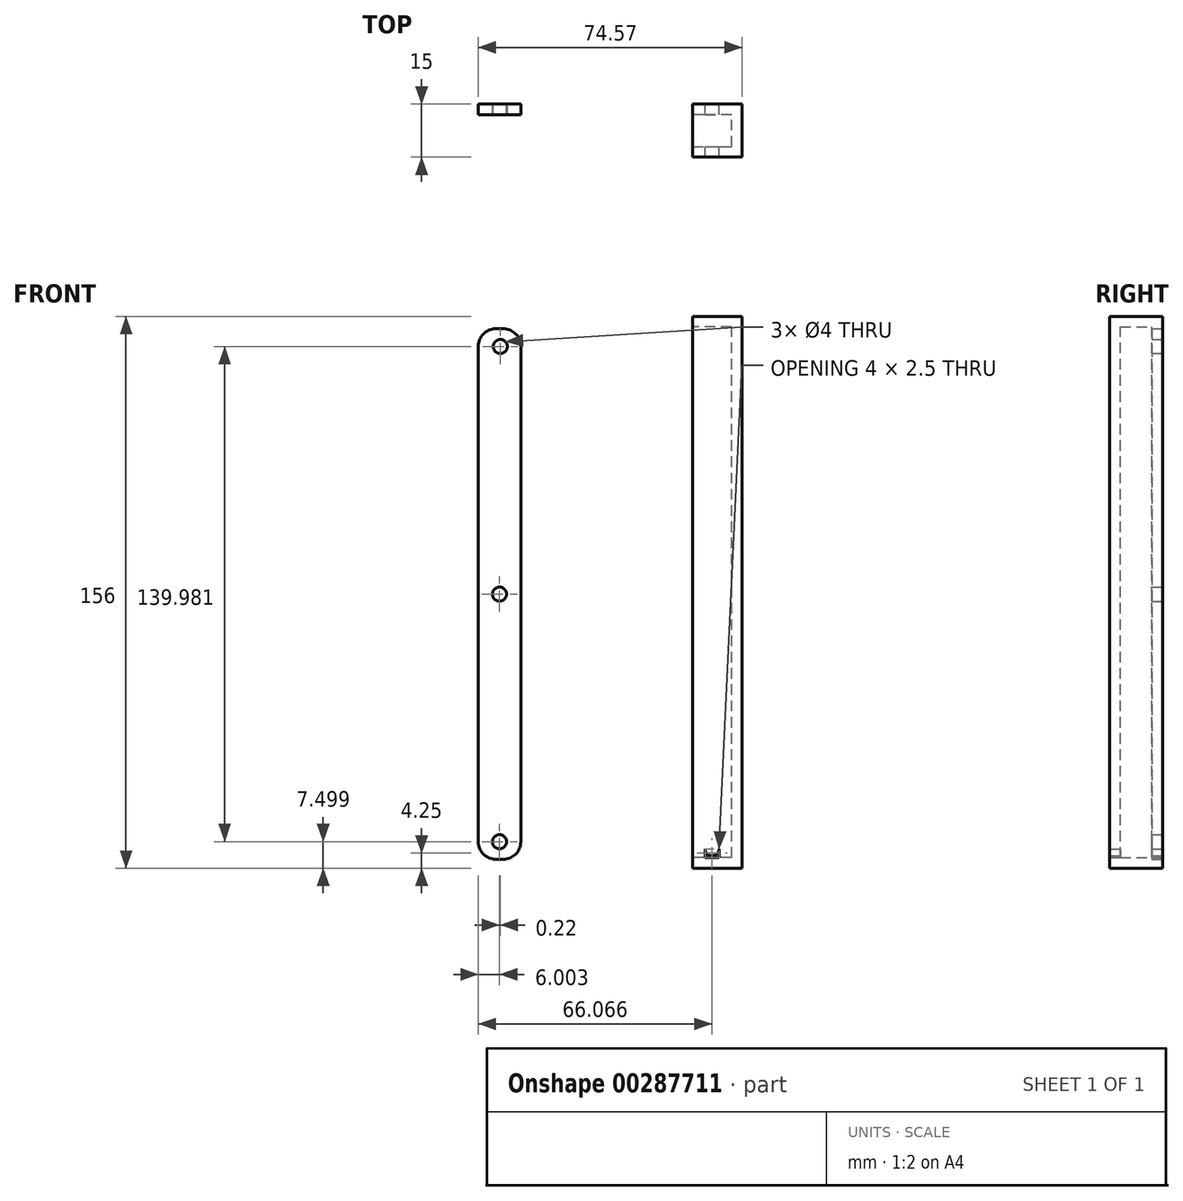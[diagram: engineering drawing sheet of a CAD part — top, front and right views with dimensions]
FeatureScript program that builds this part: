
annotation { "Feature Type Name" : "Feature", "Feature Type Description" : "" }
export const myFeature = defineFeature(function(context is Context, id is Id, definition is map)
    precondition{}
    {
        {
            var Q0;
            Q0=qCreatedBy(makeId("Front.planeOp"),FACE);
            var sketch = newSketch(context, id + "F0", { "sketchPlane" : qUnion([Q0])});
            skLineSegment(sketch, "E0.bottom", {"start": v(-38.84, 75.02) * mm, "end": v(-36.84, 75.02) * mm});
            skLineSegment(sketch, "E0.top", {"start": v(-38.84, -74.98) * mm, "end": v(-36.84, -74.98) * mm});
            skLineSegment(sketch, "E0.left", {"start": v(-43.84, 70.02) * mm, "end": v(-43.84, -69.98) * mm});
            skLineSegment(sketch, "E0.right", {"start": v(-31.84, 70.02) * mm, "end": v(-31.84, -69.98) * mm});
            skPoint(sketch, "E1.visualSharp", {"position": v(-43.84, 75.02) * mm});
            skArc(sketch, "E1.filletArc", {"start": v(-38.84, 75.02) * mm, "mid": v(-42.37, 73.55) * mm, "end": v(-43.84, 70.02) * mm});
            skPoint(sketch, "E2.visualSharp", {"position": v(-31.84, 75.02) * mm});
            skArc(sketch, "E2.filletArc", {"start": v(-31.84, 70.02) * mm, "mid": v(-33.3, 73.55) * mm, "end": v(-36.84, 75.02) * mm});
            skPoint(sketch, "E3.visualSharp", {"position": v(-43.84, -74.98) * mm});
            skArc(sketch, "E3.filletArc", {"start": v(-43.84, -69.98) * mm, "mid": v(-42.37, -73.52) * mm, "end": v(-38.84, -74.98) * mm});
            skPoint(sketch, "E4.visualSharp", {"position": v(-31.84, -74.98) * mm});
            skArc(sketch, "E4.filletArc", {"start": v(-36.84, -74.98) * mm, "mid": v(-33.3, -73.52) * mm, "end": v(-31.84, -69.98) * mm});
            skLineSegment(sketch, "E5", {"start": v(-37.84, -74.98) * mm, "end": v(-37.84, -69.98) * mm, "construction": true});
            skCircle(sketch, "E6", {"center": v(-37.84, -69.98) * mm, "radius": 2 * mm});
            skLineSegment(sketch, "E7", {"start": v(-43.84, 0.02) * mm, "end": v(-31.84, 0) * mm, "construction": true});
            skCircle(sketch, "E8.MirrorC", {"center": v(-37.62, 70) * mm, "radius": 2 * mm});
            skLineSegment(sketch, "E9.left", {"start": v(18.73, 70.52) * mm, "end": v(18.73, -69.48) * mm});
            skLineSegment(sketch, "E9.right", {"start": v(30.73, 70.02) * mm, "end": v(30.73, -69.98) * mm});
            skPoint(sketch, "E10.visualSharp", {"position": v(18.73, 75.52) * mm});
            skPoint(sketch, "E11.visualSharp", {"position": v(30.73, 75.52) * mm});
            skPoint(sketch, "E12.visualSharp", {"position": v(18.73, -74.48) * mm});
            skPoint(sketch, "E13.visualSharp", {"position": v(30.73, -74.48) * mm});
            skLineSegment(sketch, "E14", {"start": v(30.73, -69.98) * mm, "end": v(30.73, -74.48) * mm});
            skLineSegment(sketch, "E15", {"start": v(18.73, -69.48) * mm, "end": v(18.73, -74.48) * mm});
            skLineSegment(sketch, "E16", {"start": v(18.73, 70.52) * mm, "end": v(18.73, 75.52) * mm});
            skLineSegment(sketch, "E17", {"start": v(30.73, 75.52) * mm, "end": v(30.73, 70.02) * mm});
            skLineSegment(sketch, "E18", {"start": v(27.73, 75.52) * mm, "end": v(27.73, -74.98) * mm});
            skLineSegment(sketch, "E19", {"start": v(30.73, -74.48) * mm, "end": v(18.73, -74.48) * mm});
            skLineSegment(sketch, "E20", {"start": v(30.73, 75.52) * mm, "end": v(18.73, 75.52) * mm});
            skLineSegment(sketch, "E21", {"start": v(20.23, 75.52) * mm, "end": v(20.23, -74.48) * mm});
            skLineSegment(sketch, "E22", {"start": v(24.23, -74.48) * mm, "end": v(24.23, 75.52) * mm});
            skLineSegment(sketch, "E23", {"start": v(24.23, 75.52) * mm, "end": v(20.23, 75.52) * mm, "construction": true});
            skPoint(sketch, "E24.startSnap0", {"position": v(22.23, 75.52) * mm});
            skLineSegment(sketch, "E25", {"start": v(24.23, -71.98) * mm, "end": v(20.23, -71.98) * mm, "construction": true});
            skLineSegment(sketch, "E26", {"start": v(24.23, 73.02) * mm, "end": v(20.23, 73.02) * mm, "construction": true});
            skLineSegment(sketch, "E27", {"start": v(22.23, -71.98) * mm, "end": v(22.23, 73.02) * mm, "construction": true});
            skArc(sketch, "E28.0.startCap", {"start": v(24.23, -71.98) * mm, "mid": v(22.23, -73.98) * mm, "end": v(20.23, -71.98) * mm});
            skArc(sketch, "E28.0.endCap", {"start": v(20.23, 73.02) * mm, "mid": v(22.23, 75.02) * mm, "end": v(24.23, 73.02) * mm});
            skLineSegment(sketch, "E28.0.left", {"start": v(20.23, -71.98) * mm, "end": v(20.23, 73.02) * mm});
            skLineSegment(sketch, "E28.0.right", {"start": v(24.23, -71.98) * mm, "end": v(24.23, 73.02) * mm});
            skCircle(sketch, "E29", {"center": v(-37.84, 0) * mm, "radius": 2 * mm});
            skSolve(sketch);
        }
        {
            var Q0;
            Q0=makeQuery(id+"F0.imprint","IMPRINT",FACE,{"disambiguationData":[TD([[makeQuery(id+"F0.imprint","IMPRINT",EDGE,{"derivedFrom":sQuery(id+"F0.wireOp",EDGE,"E0.bottom")}),-1.0]])]});
            extrude(context, id + "F1", {"entities" : qUnion([Q0]), "depth" : 3 * mm});
        }
        {
            var Q0;
            Q0=makeQuery(id+"F0.imprint","IMPRINT",FACE,{"disambiguationData":[TD([[makeQuery(id+"F0.imprint","IMPRINT",EDGE,{"derivedFrom":sQuery(id+"F0.wireOp",EDGE,"E9.right")}),-1.0]])]});
            var Q1;
            {var subQ0=sQuery(id+"F0.wireOp",EDGE,"E18");Q1=makeQuery(id+"F0.imprint","IMPRINT",FACE,{"disambiguationData":[TD([[makeQuery(id+"F0.imprint","IMPRINT",EDGE,{"derivedFrom":subQ0}),-1.0]])]});}
            var Q2;
            {var subQ0=sQuery(id+"F0.wireOp",EDGE,"E21");Q2=makeQuery(id+"F0.imprint","IMPRINT",FACE,{"disambiguationData":[TD([[makeQuery(id+"F0.imprint","IMPRINT",EDGE,{"derivedFrom":subQ0}),1.0]])]});}
            var Q3;
            Q3=makeQuery(id+"F0.imprint","IMPRINT",FACE,{"disambiguationData":[TD([[makeQuery(id+"F0.imprint","IMPRINT",EDGE,{"derivedFrom":sQuery(id+"F0.wireOp",EDGE,"E9.left")}),1.0]])]});
            extrude(context, id + "F2", {"entities" : qUnion([Q0, Q1, Q2, Q3]), "depth" : 3 * mm});
        }
        {
            var Q0;
            Q0=makeQuery(id+"F0.imprint","IMPRINT",FACE,{"disambiguationData":[TD([[makeQuery(id+"F0.imprint","IMPRINT",EDGE,{"derivedFrom":sQuery(id+"F0.wireOp",EDGE,"E9.right")}),-1.0]])]});
            extrude(context, id + "F3", {"entities" : qUnion([Q0]), "operationType" : NewBodyOperationType.ADD, "depth" : 15 * mm});
        }
        {
            var Q0;
            {var subQ0=sQuery(id+"F0.wireOp",EDGE,"E20");Q0=makeQuery(id+"F3.boolean.opBoolean","MERGE",FACE,{"derivedFrom":[makeQuery(id+"F2.opExtrude","SWEPT_FACE",FACE,{"disambiguationData":[OSD([subQ0])]}),makeQuery(id+"F3.opExtrude","SWEPT_FACE",FACE,{"disambiguationData":[OSD([subQ0])]})]});}
            var sketch = newSketch(context, id + "F4", { "sketchPlane" : qUnion([Q0])});
            skLineSegment(sketch, "E30.0", {"start": v(27.73, -15) * mm, "end": v(27.73, -3) * mm});
            skLineSegment(sketch, "E31", {"start": v(27.73, -15) * mm, "end": v(18.73, -15) * mm});
            skLineSegment(sketch, "E32", {"start": v(18.73, -15) * mm, "end": v(18.73, -12) * mm});
            skLineSegment(sketch, "E33", {"start": v(18.73, -12) * mm, "end": v(27.73, -12) * mm});
            skSolve(sketch);
        }
        {
            var Q0;
            {var subQ0=sQuery(id+"F4.wireOp",EDGE,"E31");Q0=makeQuery(id+"F4.imprint","IMPRINT",FACE,{"disambiguationData":[TD([[makeQuery(id+"F4.imprint","IMPRINT",EDGE,{"derivedFrom":subQ0}),-1.0]])]});}
            var Q1;
            {var subQ0=sQuery(id+"F0.wireOp",EDGE,"E19");Q1=makeQuery(id+"F3.boolean.opBoolean","MERGE",FACE,{"derivedFrom":[makeQuery(id+"F2.opExtrude","SWEPT_FACE",FACE,{"disambiguationData":[OSD([subQ0])]}),makeQuery(id+"F3.opExtrude","SWEPT_FACE",FACE,{"disambiguationData":[OSD([subQ0])]})]});}
            extrude(context, id + "F5", {"entities" : qUnion([Q0]), "operationType" : NewBodyOperationType.ADD, "endBound" : BoundingType.UP_TO_SURFACE, "oppositeDirection" : true, "endBoundEntityFace" : qUnion([Q1]), "depth" : 121.1 * mm});
        }
        {
            var Q0;
            {var subQ0=sQuery(id+"F0.wireOp",EDGE,"E20");Q0=makeQuery(id+"F5.boolean.opBoolean","MERGE",FACE,{"derivedFrom":[makeQuery(id+"F3.boolean.opBoolean","MERGE",FACE,{"derivedFrom":[makeQuery(id+"F2.opExtrude","SWEPT_FACE",FACE,{"disambiguationData":[OSD([subQ0])]}),makeQuery(id+"F3.opExtrude","SWEPT_FACE",FACE,{"disambiguationData":[OSD([subQ0])]})]}),makeQuery(id+"F5.opExtrude","CAP_FACE",FACE,{"disambiguationData":[OSD([sQuery(id+"F4.wireOp",EDGE,"E30.0"),sQuery(id+"F4.wireOp",EDGE,"E31"),sQuery(id+"F4.wireOp",EDGE,"E32"),sQuery(id+"F4.wireOp",EDGE,"E33")])],"isStart":true})]});}
            var sketch = newSketch(context, id + "F6", { "sketchPlane" : qUnion([Q0])});
            skLineSegment(sketch, "E34", {"start": v(18.73, -3) * mm, "end": v(18.73, -12) * mm});
            skSolve(sketch);
        }
        {
            var Q0;
            {var subQ0=sQuery(id+"F0.wireOp",EDGE,"E20");Q0=makeQuery(id+"F6.imprint","IMPRINT",FACE,{"disambiguationData":[TD([[makeQuery(id+"F6.imprint","IMPRINT",EDGE,{"derivedFrom":makeQuery(id+"F2.opExtrude","CAP_EDGE",EDGE,{"disambiguationData":[OSD([subQ0])],"isStart":true})}),1.0]])]});}
            var Q1;
            Q1=makeQuery(id+"F6.imprint","IMPRINT",FACE,{"disambiguationData":[TD([[makeQuery(id+"F6.imprint","IMPRINT",EDGE,{"derivedFrom":sQuery(id+"F6.wireOp",EDGE,"E34")}),1.0]])]});
            extrude(context, id + "F7", {"entities" : qUnion([Q0, Q1]), "operationType" : NewBodyOperationType.ADD, "depth" : 3 * mm});
        }
        {
            var Q0;
            Q0=makeQuery(id+"F7.opExtrude","CAP_FACE",FACE,{"disambiguationData":[OSD([sQuery(id+"F0.wireOp",EDGE,"E16"),sQuery(id+"F0.wireOp",EDGE,"E17"),sQuery(id+"F0.wireOp",EDGE,"E20"),sQuery(id+"F4.wireOp",EDGE,"E31"),sQuery(id+"F4.wireOp",EDGE,"E32"),sQuery(id+"F6.wireOp",EDGE,"E34")])],"isStart":false});
            var Q1;
            {var subQ0=sQuery(id+"F0.wireOp",EDGE,"E19");Q1=makeQuery(id+"F5.boolean.opBoolean","MERGE",FACE,{"derivedFrom":[makeQuery(id+"F3.boolean.opBoolean","MERGE",FACE,{"derivedFrom":[makeQuery(id+"F2.opExtrude","SWEPT_FACE",FACE,{"disambiguationData":[OSD([subQ0])]}),makeQuery(id+"F3.opExtrude","SWEPT_FACE",FACE,{"disambiguationData":[OSD([subQ0])]})]}),makeQuery(id+"F5.opExtrude","CAP_FACE",FACE,{"disambiguationData":[OSD([subQ0])],"isStart":false})]});}
            var Q2;
            {var subQ0=sQuery(id+"F0.wireOp",EDGE,"E19");Q2=makeQuery(id+"F5.boolean.opBoolean","MERGE",FACE,{"derivedFrom":[makeQuery(id+"F3.boolean.opBoolean","MERGE",FACE,{"derivedFrom":[makeQuery(id+"F2.opExtrude","SWEPT_FACE",FACE,{"disambiguationData":[OSD([subQ0])]}),makeQuery(id+"F3.opExtrude","SWEPT_FACE",FACE,{"disambiguationData":[OSD([subQ0])]})]}),makeQuery(id+"F5.opExtrude","CAP_FACE",FACE,{"disambiguationData":[OSD([subQ0])],"isStart":false})]});}
            extrude(context, id + "F8", {"entities" : qUnion([Q0]), "operationType" : NewBodyOperationType.ADD, "oppositeDirection" : true, "endBoundEntityFace" : qUnion([Q1]), "depth" : 156 * mm, "hasSecondDirection" : true, "secondDirectionBound" : SecondDirectionBoundingType.UP_TO_SURFACE, "secondDirectionOppositeDirection" : true, "secondDirectionBoundEntityFace" : qUnion([Q2]), "secondDirectionDepth" : 156 * mm});
        }
        {
            var Q0;
            Q0=makeQuery(id+"F0.imprint","IMPRINT",FACE,{"disambiguationData":[TD([[makeQuery(id+"F0.imprint","IMPRINT",EDGE,{"derivedFrom":sQuery(id+"F0.wireOp",EDGE,"E28.0.startCap")}),-1.0]])]});
            var Q1;
            {var subQ0=sQuery(id+"F4.wireOp",EDGE,"E31");var subQ1=sQuery(id+"F0.wireOp",EDGE,"E20");Q1=makeQuery(id+"F8.boolean.opBoolean","MERGE",FACE,{"derivedFrom":[makeQuery(id+"F7.boolean.opBoolean","MERGE",FACE,{"derivedFrom":[makeQuery(id+"F5.boolean.opBoolean","MERGE",FACE,{"derivedFrom":[makeQuery(id+"F3.opExtrude","CAP_FACE",FACE,{"disambiguationData":[OSD([sQuery(id+"F0.wireOp",EDGE,"E9.right"),sQuery(id+"F0.wireOp",EDGE,"E14"),sQuery(id+"F0.wireOp",EDGE,"E17"),sQuery(id+"F0.wireOp",EDGE,"E18"),sQuery(id+"F0.wireOp",EDGE,"E19"),subQ1])],"isStart":false}),makeQuery(id+"F5.opExtrude","SWEPT_FACE",FACE,{"disambiguationData":[OSD([subQ0])]})]}),makeQuery(id+"F7.opExtrude","SWEPT_FACE",FACE,{"disambiguationData":[OSD([subQ1,subQ0])]})]}),makeQuery(id+"F8.opExtrude","SWEPT_FACE",FACE,{"disambiguationData":[OSD([subQ1,subQ0])]})]});}
            extrude(context, id + "F9", {"entities" : qUnion([Q0]), "operationType" : NewBodyOperationType.REMOVE, "endBound" : BoundingType.UP_TO_SURFACE, "endBoundEntityFace" : qUnion([Q1]), "depth" : 25 * mm});
        }
        {
            var Q0;
            {var subQ0=sQuery(id+"F6.wireOp",EDGE,"E34");var subQ1=sQuery(id+"F4.wireOp",EDGE,"E32");var subQ2=sQuery(id+"F0.wireOp",EDGE,"E20");var subQ3=sQuery(id+"F0.wireOp",EDGE,"E16");Q0=makeQuery(id+"F8.boolean.opBoolean","MERGE",FACE,{"derivedFrom":[makeQuery(id+"F7.boolean.opBoolean","MERGE",FACE,{"derivedFrom":[makeQuery(id+"F2.opExtrude","SWEPT_FACE",FACE,{"disambiguationData":[OSD([sQuery(id+"F0.wireOp",EDGE,"E9.left"),sQuery(id+"F0.wireOp",EDGE,"E15"),subQ3])]}),makeQuery(id+"F5.opExtrude","SWEPT_FACE",FACE,{"disambiguationData":[OSD([subQ1])]}),makeQuery(id+"F7.opExtrude","SWEPT_FACE",FACE,{"disambiguationData":[OSD([subQ3,subQ2,subQ1,subQ0])]})]}),makeQuery(id+"F8.opExtrude","SWEPT_FACE",FACE,{"disambiguationData":[OSD([subQ3,subQ2,subQ1,subQ0])]})]});}
            extrude(context, id + "F10", {"entities" : qUnion([Q0]), "operationType" : NewBodyOperationType.ADD, "depth" : 2 * mm});
        }
    });
